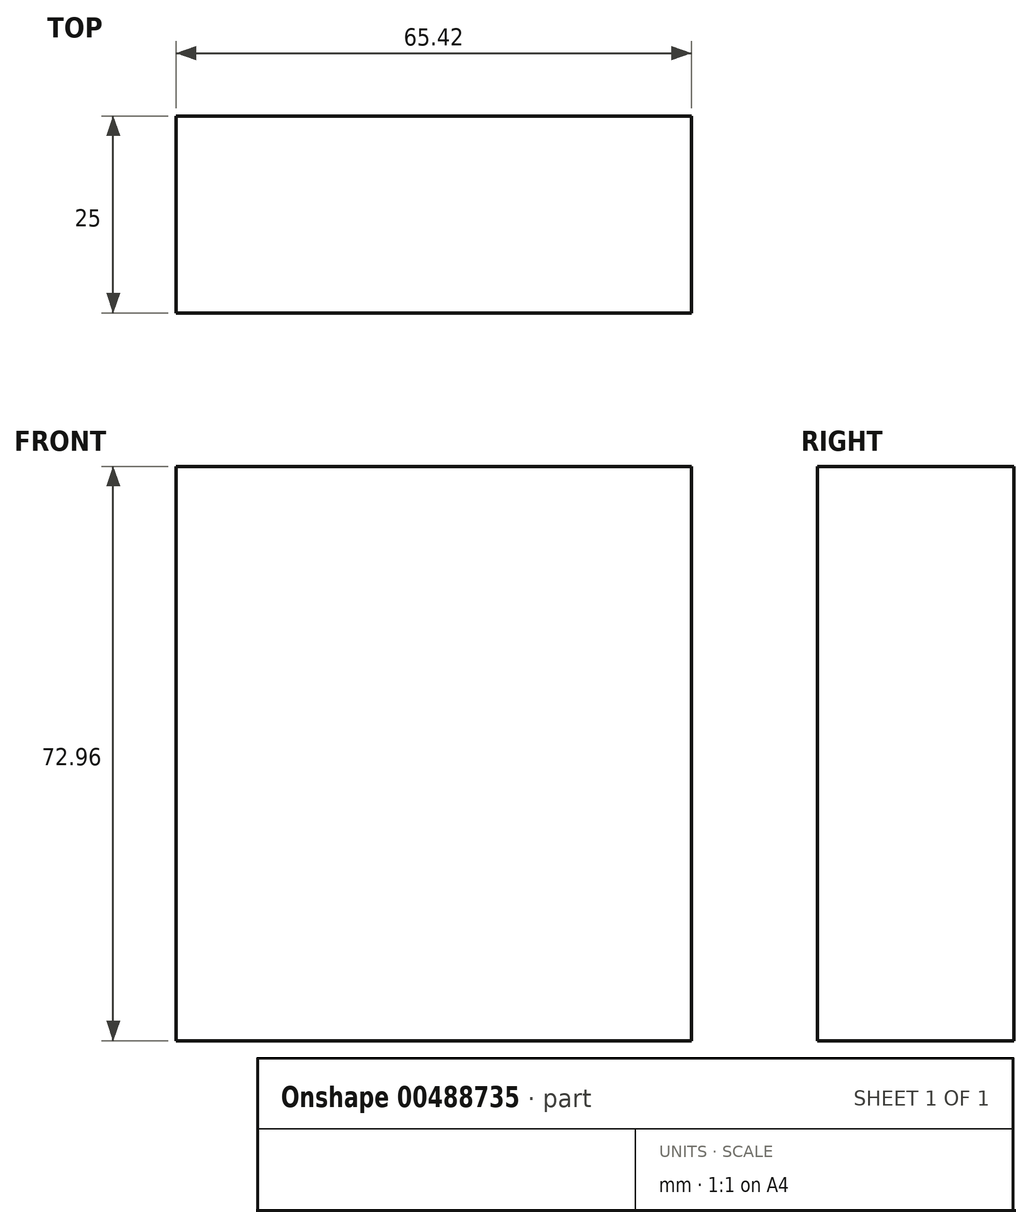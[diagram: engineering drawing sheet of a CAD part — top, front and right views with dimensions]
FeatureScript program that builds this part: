
annotation { "Feature Type Name" : "Feature", "Feature Type Description" : "" }
export const myFeature = defineFeature(function(context is Context, id is Id, definition is map)
    precondition{}
    {
        {
            var Q0;
            Q0=qCreatedBy(makeId("Front.planeOp"),FACE);
            var sketch = newSketch(context, id + "F0", { "sketchPlane" : qUnion([Q0])});
            skLineSegment(sketch, "E0.bottom", {"start": v(-111.82, 12.11) * mm, "end": v(-46.4, 12.11) * mm});
            skLineSegment(sketch, "E0.top", {"start": v(-111.82, 85.07) * mm, "end": v(-46.4, 85.07) * mm});
            skLineSegment(sketch, "E0.left", {"start": v(-111.82, 12.11) * mm, "end": v(-111.82, 85.07) * mm});
            skLineSegment(sketch, "E0.right", {"start": v(-46.4, 12.11) * mm, "end": v(-46.4, 85.07) * mm});
            skPoint(sketch, "E0.middle", {"position": v(-79.1, 48.6) * mm});
            skSolve(sketch);
        }
        {
            var Q0;
            Q0=makeQuery(id+"F0.imprint","IMPRINT",FACE,{"disambiguationData":[TD([[makeQuery(id+"F0.imprint","IMPRINT",EDGE,{"derivedFrom":sQuery(id+"F0.wireOp",EDGE,"E0.bottom")}),1.0]])]});
            extrude(context, id + "F1", {"entities" : qUnion([Q0]), "depth" : 25 * mm});
        }
    });
